# Revit family: Spout-BathSpout-WithHandshowerOutlet-Vitra-RootSeries-A42719
name_source: partatom
category: Plumbing Fixtures
revit_build: Autodesk Revit 2017 (Build: 20160225_1515(x64)
units: mm (PartAtom-declared; Revit-internal decimal feet)

## family parameters
Cut with Voids When Loaded = No
Host = Face
OmniClass Number = 23.45.55.17
OmniClass Title = Mixing Faucets
Part Type = Normal
Room Calculation Point = No
Round Connector Dimension = Use Diameter
Shared = Yes

## types (8) — shared parameters
BIMobject category = Bath/Shower Mixer
CW Connection = Yes
Connection Diameter (mm) = 15 mm  [stored 0.0492126 ft]
Default Elevation = 850 mm  [stored 2.78871 ft]
Description = Root Round Wall-Mounted Bath Spout
Design country = Turkey
HW Connection = Yes
Hot Water Supply (max.) = 80 °C
Hot Water temperature, factory set to = 38 °C
IFC Classification = Sanitary Terminal
Main Material = Brass
Manufacturer = Vitra
Manufacturer name = Vitra
Masterformat 2014 Code = 22 40 00
Masterformat 2014 Description = Plumbing Fixtures
Min. flow pressure of = 0.5 bar
Mounting type = Wall-mounted (exposed part)
NBS Referans Code = 45-35-70/371
NBS Referans Description = Water supply fittings for wash basins and troughs
Nominal Depth (mm) = 200 mm  [stored 0.656168 ft]
Nominal Height (mm) = 85 mm  [stored 0.278871 ft]
Nominal Width (mm) = 85 mm  [stored 0.278871 ft]
Number Of Connections = 1
OmniClass Code = 23.45.55.17
OmniClass Description = Mixing Faucets
Product Type = Spout
Product certification = https://www.vitraglobal.com
Product family = Built-in bath/shower mixer (exposed part)
Product group = Root Round Spout
Range of Hot Water Supply = 5 - 65 °C
Range of flow pressure = 1 - 5 bar
Test Pressure = 16 bar
UNSPSC Code = 301815
URL = https://vitraglobal.com
Uniclass 1.4 Code = L725111
Uniclass 1.4 Description = Mixer taps
Uniclass 2.0 Code = Pr_40_20_87_09
Uniclass 2.0 Description = Mixer taps
Uniclass 2015 Code = Pr_40_20_87_98
Uniclass 2015 Name = Bath taps
Uniformat II Code = 22 40 00
Uniformat II Description = Plumbing Fixture
Vent Connection = No
Warranty Period (Year) = 10 Years
Waste Connection = No
Weight Net (kg) = 1
Youtube = https://www.youtube.com

## per-type parameters (varying)
| type | Article No. (default) | Brand | Coating Material | Color | Model | Product SKU | Product url | Technical description |
| Spout-BathSpout-WithHandshowerOutlet-Vitra-RootSeries-A42719 | A42719 | Artema | Chrome | Chrome | A42719 | A42719 | https://www.vitra.com.tr | https://www.vitra.com.tr |
| Spout-BathSpout-WithHandshowerOutlet-Vitra-RootSeries-A4271923 | A4271923 | Artema | Gold | Gold | A4271923 | A4271923 | https://www.vitra.com.tr | https://www.vitra.com.tr |
| Spout-BathSpout-WithHandshowerOutlet-Vitra-RootSeries-A4271926 | A4271926 | Artema | Copper | Copper | A4271926 | A4271926 | https://www.vitra.com.tr | https://www.vitra.com.tr |
| Spout-BathSpout-WithHandshowerOutlet-Vitra-RootSeries-A4271934 | A4271934 | Artema | Nickel (Metal) | Nickel | A4271934 | A4271934 | https://www.vitra.com.tr | https://www.vitra.com.tr |
| Spout-BathSpout-WithHandshowerOutlet-Vitra-RootSeries-A42719EXP | A42719EXP | VitrA | Chrome | Chrome | A42719EXP | A42719EXP | https://www.vitraglobal.com | https://www.vitraglobal.com |
| Spout-BathSpout-WithHandshowerOutlet-Vitra-RootSeries-A4271923EXP | A4271923EXP | VitrA | Gold | Gold | A4271923EXP | A4271923EXP | https://www.vitraglobal.com | https://www.vitraglobal.com |
| Spout-BathSpout-WithHandshowerOutlet-Vitra-RootSeries-A4271926EXP | A4271926EXP | VitrA | Copper | Copper | A4271926EXP | A4271926EXP | https://www.vitraglobal.com | https://www.vitraglobal.com |
| Spout-BathSpout-WithHandshowerOutlet-Vitra-RootSeries-A4271934EXP | A4271934EXP | VitrA | Nickel (Metal) | Nickel | A4271934EXP | A4271934EXP | https://www.vitraglobal.com | https://www.vitraglobal.com |

note: [stored X ft] marks values corroborated as IEEE doubles in the binary element streams (Revit-internal decimal feet)

## geometry (parser evidence)
native form markers: Sweep x2
no freeform markers — native parametric forms only
